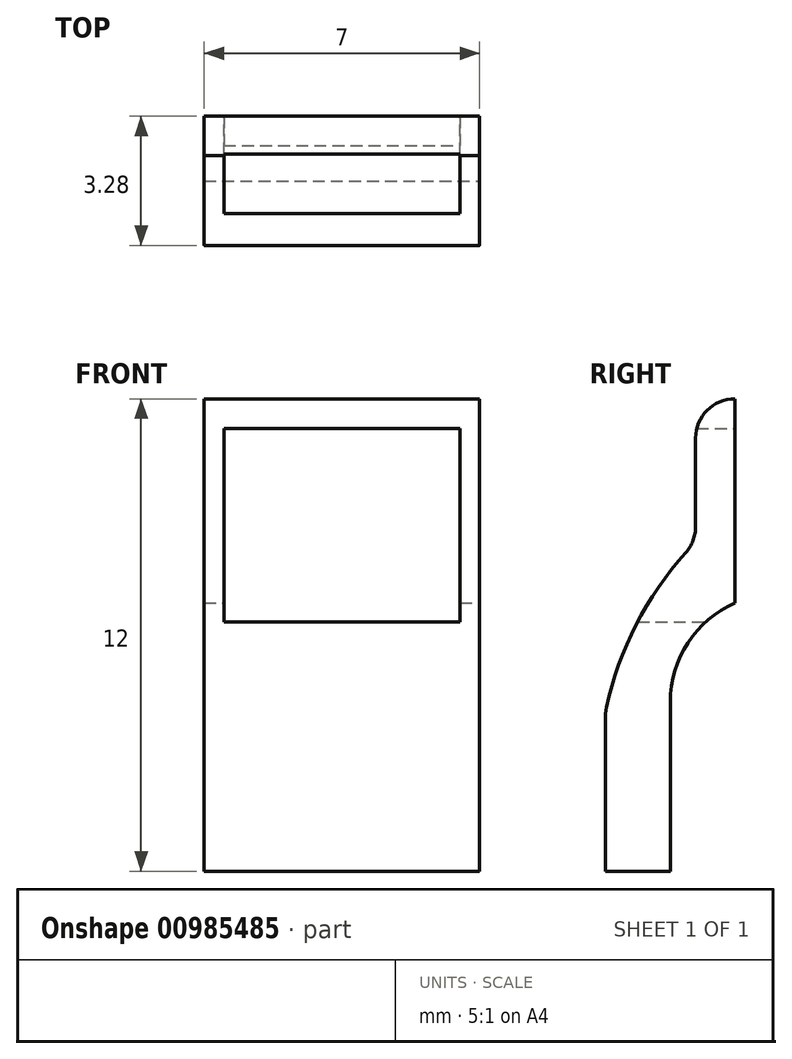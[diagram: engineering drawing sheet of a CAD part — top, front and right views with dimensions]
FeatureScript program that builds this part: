
annotation { "Feature Type Name" : "Feature", "Feature Type Description" : "" }
export const myFeature = defineFeature(function(context is Context, id is Id, definition is map)
    precondition{}
    {
        {
            var Q0;
            Q0=qCreatedBy(makeId("Right.planeOp"),FACE);
            var sketch = newSketch(context, id + "F0", { "sketchPlane" : qUnion([Q0])});
            skLineSegment(sketch, "E0", {"start": v(-0.07, 0.58) * mm, "end": v(-0.07, 12.58) * mm});
            skLineSegment(sketch, "E1", {"start": v(-0.07, 12.58) * mm, "end": v(-0.07, 12.58) * mm});
            skLineSegment(sketch, "E2", {"start": v(-1.07, 11.58) * mm, "end": v(-1.07, 9.34) * mm});
            skArc(sketch, "E3", {"start": v(-1.32, 8.67) * mm, "mid": v(-2.58, 6.84) * mm, "end": v(-3.33, 4.75) * mm});
            skLineSegment(sketch, "E4", {"start": v(-3.35, 4.53) * mm, "end": v(-3.35, 0.58) * mm});
            skLineSegment(sketch, "E5", {"start": v(-3.35, 0.58) * mm, "end": v(-0.07, 0.58) * mm});
            skPoint(sketch, "E6.visualSharp", {"position": v(-1.07, 8.94) * mm});
            skArc(sketch, "E6.filletArc", {"start": v(-1.32, 8.67) * mm, "mid": v(-1.13, 8.98) * mm, "end": v(-1.07, 9.34) * mm});
            skPoint(sketch, "E7.visualSharp", {"position": v(-1.07, 12.58) * mm});
            skArc(sketch, "E7.filletArc", {"start": v(-0.07, 12.58) * mm, "mid": v(-0.77, 12.29) * mm, "end": v(-1.07, 11.58) * mm});
            skPoint(sketch, "E8.visualSharp", {"position": v(-3.35, 4.64) * mm});
            skArc(sketch, "E8.filletArc", {"start": v(-3.33, 4.75) * mm, "mid": v(-3.35, 4.64) * mm, "end": v(-3.35, 4.53) * mm});
            skSolve(sketch);
        }
        {
            var Q0;
            Q0=qSketchRegion(id+"F0",true);
            extrude(context, id + "F1", {"entities" : qUnion([Q0]), "depth" : 7 * mm});
        }
        {
            var Q0;
            Q0=makeQuery(id+"F1.opExtrude","SWEPT_FACE",FACE,{"disambiguationData":[OSD([sQuery(id+"F0.wireOp",EDGE,"E0")])]});
            var sketch = newSketch(context, id + "F2", { "sketchPlane" : qUnion([Q0])});
            skLineSegment(sketch, "E9.bottom", {"start": v(-6.5, 11.83) * mm, "end": v(-0.5, 11.83) * mm});
            skLineSegment(sketch, "E9.top", {"start": v(-6.5, 6.91) * mm, "end": v(-0.5, 6.91) * mm});
            skLineSegment(sketch, "E9.left", {"start": v(-6.5, 11.83) * mm, "end": v(-6.5, 6.91) * mm});
            skLineSegment(sketch, "E9.right", {"start": v(-0.5, 11.83) * mm, "end": v(-0.5, 6.91) * mm});
            skSolve(sketch);
        }
        {
            var Q0;
            Q0=qSketchRegion(id+"F2",true);
            extrude(context, id + "F3", {"entities" : qUnion([Q0]), "operationType" : NewBodyOperationType.REMOVE, "endBound" : BoundingType.THROUGH_ALL, "oppositeDirection" : true, "depth" : 25 * mm});
        }
        {
            var Q0;
            Q0=makeQuery(id+"F1.opExtrude","CAP_FACE",FACE,{"disambiguationData":[OSD([sQuery(id+"F0.wireOp",EDGE,"E0"),sQuery(id+"F0.wireOp",EDGE,"E2"),sQuery(id+"F0.wireOp",EDGE,"E3"),sQuery(id+"F0.wireOp",EDGE,"E4"),sQuery(id+"F0.wireOp",EDGE,"E5"),sQuery(id+"F0.wireOp",EDGE,"E6.filletArc"),sQuery(id+"F0.wireOp",EDGE,"E7.filletArc"),sQuery(id+"F0.wireOp",EDGE,"E8.filletArc")])],"isStart":false});
            var sketch = newSketch(context, id + "F4", { "sketchPlane" : qUnion([Q0])});
            skLineSegment(sketch, "E10.bottom", {"start": v(-1.7, 0.58) * mm, "end": v(-0.07, 0.58) * mm});
            skLineSegment(sketch, "E10.left", {"start": v(-1.7, 0.58) * mm, "end": v(-1.7, 4.89) * mm});
            skLineSegment(sketch, "E10.right", {"start": v(-0.07, 0.58) * mm, "end": v(-0.07, 2.01) * mm});
            skArc(sketch, "E11", {"start": v(-0.07, 7.4) * mm, "mid": v(-1.26, 6.39) * mm, "end": v(-1.7, 4.89) * mm});
            skLineSegment(sketch, "E12", {"start": v(-0.07, 7.4) * mm, "end": v(-0.07, 2.01) * mm});
            skSolve(sketch);
        }
        {
            var Q0;
            Q0=qSketchRegion(id+"F4",true);
            extrude(context, id + "F5", {"entities" : qUnion([Q0]), "operationType" : NewBodyOperationType.REMOVE, "endBound" : BoundingType.THROUGH_ALL, "oppositeDirection" : true, "depth" : 25 * mm});
        }
    });
